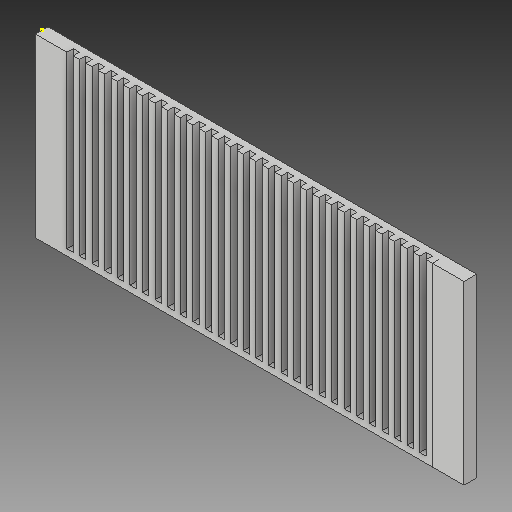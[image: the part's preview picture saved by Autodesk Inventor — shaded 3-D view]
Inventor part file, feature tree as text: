
AUTODESK INVENTOR PART (.ipt)
format: ipt  version: 2017 (Build 210142000, 142)  size: 534,016 bytes
history: native  units: in
note: dims shown in document units (in); Inventor stores cm internally (conversion verified against a paired STEP export)
features: sketch x35, extrude x34, pattern_linear x13
ambient origin geometry x8: Origin, YZ Plane, XZ Plane, XY Plane, X Axis, Y Axis, Z Axis, Center Point
bodies: Solid1 (feature_tree)
feature tree (82):
  extrude  "Extrusion1"  Depth=3.5in
  extrude  "Extrusion2"  Depth=0.625in
  extrude  "Extrusion3"  Depth=0.125in TaperAngle=0.0deg
  extrude  "Extrusion4"  Depth=0.125in
  extrude  "Extrusion5"  Depth=0.125in
  sketch  "Sketch6"  dims[d13=3.5in d14=0.125in d15=0.0in]
  extrude  "Extrusion6"  Depth=0.125in TaperAngle=0.0deg
  extrude  "Extrusion7"  Depth=0.125in
  extrude  "Extrusion8"  Depth=0.125in
  extrude  "Extrusion9"  Depth=0.125in TaperAngle=0.0deg
  extrude  "Extrusion10"  Depth=0.125in
  extrude  "Extrusion11"  Depth=0.125in
  extrude  "Extrusion12"  Depth=0.125in TaperAngle=0.0deg
  extrude  "Extrusion13"  Depth=3.5in
  extrude  "Extrusion14"  Depth=0.125in
  extrude  "Extrusion15"  Depth=0.125in TaperAngle=0.0deg
  extrude  "Extrusion16"  Depth=3.5in
  extrude  "Extrusion17"  Depth=0.125in
  extrude  "Extrusion18"  Depth=0.125in TaperAngle=0.0deg
  extrude  "Extrusion19"  Depth=3.5in
  extrude  "Extrusion20"  Depth=0.125in
  extrude  "Extrusion21"  Depth=0.125in TaperAngle=0.0deg
  extrude  "Extrusion22"  Depth=3.5in
  extrude  "Extrusion23"  Depth=0.125in
  extrude  "Extrusion24"  Depth=0.125in TaperAngle=0.0deg
  extrude  "Extrusion25"  Depth=3.5in
  extrude  "Extrusion26"  Depth=0.125in
  extrude  "Extrusion27"  Depth=0.125in TaperAngle=0.0deg
  extrude  "Extrusion28"  Depth=3.5in
  extrude  "Extrusion29"  Depth=0.125in
  extrude  "Extrusion30"  Depth=0.125in TaperAngle=0.0deg
  extrude  "Extrusion31"  Depth=3.5in
  extrude  "Extrusion32"  Depth=0.125in
  extrude  "Extrusion33"  Depth=0.125in TaperAngle=0.0deg
  extrude  "Extrusion34"  Depth=3.5in
  pattern_linear  "Rectangular Pattern1"  Spacing1=0.125in  [1 undecoded]
  pattern_linear  "Rectangular Pattern2"  Spacing1=0.125in  [1 undecoded]
  pattern_linear  "Rectangular Pattern3"  Spacing1=0.125in  [1 undecoded]
  pattern_linear  "Rectangular Pattern4"  Spacing1=0.125in  [1 undecoded]
  pattern_linear  "Rectangular Pattern5"  Spacing1=3.5in  [1 undecoded]
  pattern_linear  "Rectangular Pattern6"  Spacing1=0.125in  [1 undecoded]
  pattern_linear  "Rectangular Pattern7"  Spacing1=0.125in  [1 undecoded]
  pattern_linear  "Rectangular Pattern8"  Spacing1=0.125in  [1 undecoded]
  pattern_linear  "Rectangular Pattern9"  Spacing1=0.125in  [1 undecoded]
  pattern_linear  "Rectangular Pattern10"  Spacing1=0.125in  [1 undecoded]
  pattern_linear  "Rectangular Pattern11"  Spacing1=3.5in  [1 undecoded]
  pattern_linear  "Rectangular Pattern12"  Spacing1=0.125in  [1 undecoded]
  pattern_linear  "Rectangular Pattern13"  Spacing1=0.125in  [1 undecoded]
  sketch  "Sketch1"  dims[d0=8.5in d1=3.5in]
  sketch  "Sketch2"  dims[d2=0.125in d3=0.0in d4=0.625in]
  sketch  "Sketch3"  dims[d5=3.5in d6=0.125in d7=0.0in]
  sketch  "Sketch4"  dims[d8=0.125in d9=0.125in]
  sketch  "Sketch5"  dims[d10=0.125in d11=0.0in d12=0.125in]
  sketch  "Sketch7"  dims[d16=0.125in d17=0.125in]
  sketch  "Sketch8"  dims[d18=0.125in d19=0.0in d20=0.125in]
  sketch  "Sketch9"  dims[d21=3.5in d22=0.125in d23=0.0in]
  sketch  "Sketch10"  dims[d24=0.125in d25=0.125in]
  sketch  "Sketch11"  dims[d26=0.125in d27=0.0in d28=0.125in]
  sketch  "Sketch12"  dims[d29=3.5in d30=0.125in d31=0.0in]
  sketch  "Sketch13"  dims[d32=0.625in d33=3.5in]
  sketch  "Sketch14"  dims[d34=0.125in d35=0.0in d36=0.125in]
  sketch  "Sketch15"  dims[d37=0.125in d38=0.125in d39=0.0in]
  sketch  "Sketch16"  dims[d40=0.125in d41=3.5in]
  sketch  "Sketch17"  dims[d42=0.125in d43=0.0in d44=0.125in]
  sketch  "Sketch18"  dims[d45=0.125in d46=0.125in d47=0.0in]
  sketch  "Sketch19"  dims[d48=0.125in d49=3.5in]
  sketch  "Sketch20"  dims[d50=0.125in d51=0.0in d52=0.125in]
  sketch  "Sketch21"  dims[d53=0.125in d54=0.125in d55=0.0in]
  sketch  "Sketch22"  dims[d56=0.125in d57=3.5in]
  sketch  "Sketch23"  dims[d58=0.125in d59=0.0in d60=0.125in]
  sketch  "Sketch24"  dims[d61=0.125in d62=0.125in d63=0.0in]
  sketch  "Sketch25"  dims[d64=0.125in d65=3.5in]
  sketch  "Sketch26"  dims[d66=0.125in d67=0.0in d68=0.125in]
  sketch  "Sketch27"  dims[d69=0.125in d70=0.125in d71=0.0in]
  sketch  "Sketch28"  dims[d72=0.125in d73=3.5in]
  sketch  "Sketch29"  dims[d74=0.125in d75=0.0in d76=0.125in]
  sketch  "Sketch30"  dims[d77=0.125in d78=0.125in d79=0.0in]
  sketch  "Sketch31"  dims[d80=0.125in d81=3.5in]
  sketch  "Sketch32"  dims[d82=0.125in d83=0.0in d84=0.125in]
  sketch  "Sketch33"  dims[d85=0.125in d86=0.125in d87=0.0in]
  sketch  "Sketch34"  dims[d88=0.125in d89=3.5in]
  sketch  "Sketch35"  dims[d90=0.125in d91=0.0in d92=0.125in d93=0.125in d94=0.125in d95=0.0in d96=0.125in d97=3.5in d98=0.125in d99=0.0in d100=0.125in d101=0.125in d102=0.125in d103=0.0in d104=0.125in d105=3.5in d106=0.125in d107=0.0in d108=0.125in d109=0.125in d110=0.125in d111=0.0in d112=0.125in d113=3.5in d114=0.125in d115=0.0in d116=0.125in d117=0.125in d118=0.0in d119=0.125in d120=3.5in d121=0.125in d122=0.0in d123=0.125in d124=0.125in d125=0.125in d126=0.0in d127=0.125in d128=3.5in d129=0.125in d130=0.0in d131=0.125in d132=0.125in d133=0.125in d134=0.0in d135=0.7874in d137=0.25in d138=0.7874in d140=0.25in d141=0.7874in d143=0.5in d144=0.7874in d146=0.5in d147=0.7874in d149=1.0in d150=0.7874in d152=1.0in d153=0.7874in d155=2.25in d156=0.7874in d158=3.0in d159=0.7874in d161=2.0in d162=0.7874in d164=3.5in d165=0.7874in d167=4.5in d168=0.7874in d170=2.5in d171=0.7874in d173=4.25in]
note: 13 required parameter values undecoded (feature->parameter linkage not recoverable at this tier; creation-order binding heuristic only, values carry confidence <= 0.55)
